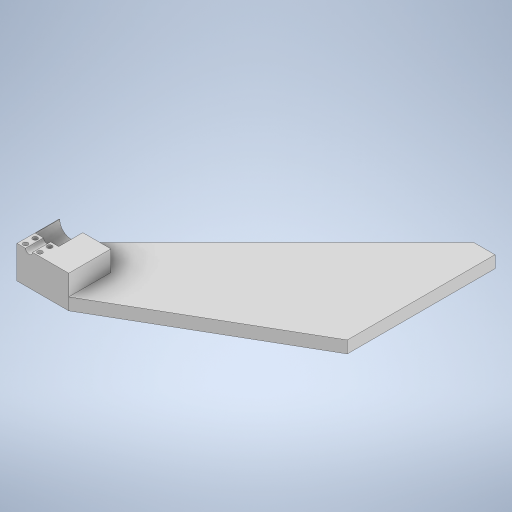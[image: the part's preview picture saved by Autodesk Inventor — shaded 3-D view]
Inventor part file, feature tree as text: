
AUTODESK INVENTOR PART (.ipt)
format: ipt  version: 2024 (Build 280153000, 153)  size: 285,184 bytes
history: native  units: mm
features: extrude x8, sketch x8
ambient origin geometry x8: Origin, YZ Plane, XZ Plane, XY Plane, X Axis, Y Axis, Z Axis, Center Point
bodies: Solid1 (feature_tree)
feature tree (16):
  extrude  "Extrusion1"  Depth=230.0mm
  extrude  "Extrusion2"  Depth=35.0mm
  extrude  "Extrusion3"  Depth=17.0mm TaperAngle=0.0deg
  extrude  "Extrusion4"  Depth=20.0mm TaperAngle=0.0deg
  extrude  "Extrusion5"  Depth=40.0mm TaperAngle=0.0deg
  extrude  "Extrusion6"  Depth=40.0mm TaperAngle=0.0deg
  extrude  "Extrusion7"  Depth=10.0mm
  extrude  "Extrusion8"  [1 undecoded]
  sketch  "Sketch1"  dims[d0=175.0mm d1=230.0mm]
  sketch  "Sketch2"  dims[d2=45.0deg d3=35.0mm]
  sketch  "Sketch3"  dims[d4=10.0mm d5=0.0mm d6=17.0mm d7=0.0mm]
  sketch  "Sketch4"  dims[d8=40.0mm d9=0.0mm d10=20.0mm d11=0.0mm]
  sketch  "Sketch5"  dims[d12=5.8mm d14=40.0mm d15=0.0mm]
  sketch  "Sketch6"  dims[d18=30.0deg d19=40.0mm d20=0.0mm]
  sketch  "Sketch7"  dims[d21=10.0mm d22=0.0mm d23=40.5mm]
  sketch  "Sketch8"  dims[d24=10.0mm d25=0.0mm]
note: 1 required parameter value undecoded (feature->parameter linkage not recoverable at this tier; creation-order binding heuristic only, values carry confidence <= 0.55)
